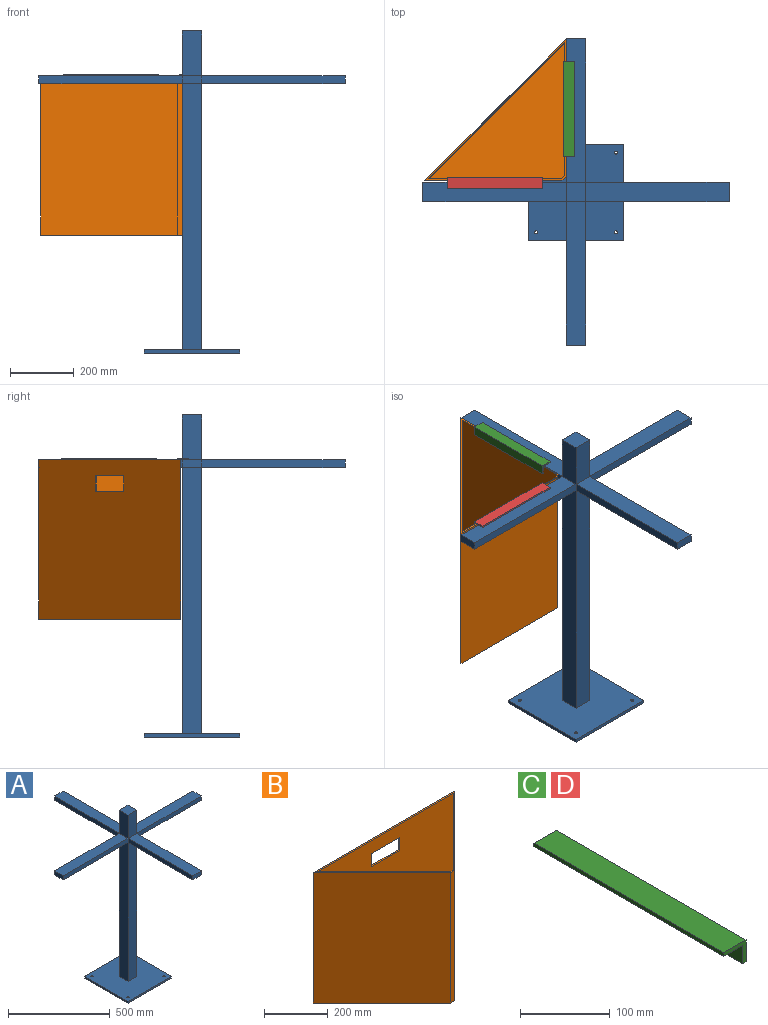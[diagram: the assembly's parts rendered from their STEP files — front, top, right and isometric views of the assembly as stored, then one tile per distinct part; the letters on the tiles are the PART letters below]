
ASSEMBLY  parts=4 mates=3
PART A: 39 faces, bbox 960x960x1010 mm
  f0: plane 835x60mm, normal (0,1,0), area 50100mm2, adj f1,f3,f13,f19
  f1: plane 835x60mm, normal (-1,0,0), area 50100mm2, adj f0,f2,f13,f17
  f2: plane 835x60mm, normal (0,-1,0), area 50100mm2, adj f1,f3,f13,f18
  f3: plane 835x60mm, normal (1,0,0), area 50100mm2, adj f0,f2,f13,f25
  f4: plane 300x10mm, normal (0,1,0), area 3000mm2, adj f5,f11,f12,f13
  f5: plane 300x10mm, normal (-1,0,0), area 3000mm2, adj f4,f6,f12,f13
  f6: plane 300x10mm, normal (0,-1,0), area 3000mm2, adj f5,f11,f12,f13
  f7: cylinder r=5mm len=10mm, axis (0,0,1), area 314.2mm2, adj f12,f13
  f8: cylinder r=5mm len=10mm, axis (0,0,1), area 314.2mm2, adj f12,f13
  f9: cylinder r=5mm len=10mm, axis (0,0,1), area 314.2mm2, adj f12,f13
  f10: cylinder r=5mm len=10mm, axis (0,0,1), area 314.2mm2, adj f12,f13
  f11: plane 300x10mm, normal (1,0,0), area 3000mm2, adj f4,f6,f12,f13
  f12: plane 300x300mm, normal (0,0,-1), area 89685.8mm2, adj f4,f5,f6,f7,f8,f9,f10,f11
  f13: plane 300x300mm, normal (0,0,1), area 86085.8mm2, adj f0,f1,f2,f3,f4,f5,f6,f7
  f14: plane 450x60mm, normal (0,0,1), area 27000mm2, adj f28,f29,f30,f37
  f15: plane 450x60mm, normal (0,0,1), area 27000mm2, adj f20,f21,f26,f36
  f16: plane 450x60mm, normal (0,0,1), area 27000mm2, adj f22,f24,f27,f38
  f17: plane 450x60mm, normal (0,0,-1), area 27000mm2, adj f1,f28,f29,f30
  f18: plane 450x60mm, normal (0,0,-1), area 27000mm2, adj f2,f20,f21,f26
  f19: plane 450x60mm, normal (0,0,-1), area 27000mm2, adj f0,f22,f24,f27
  f20: plane 450x25mm, normal (1,0,0), area 11250mm2, adj f15,f18,f26,f32
  f21: plane 450x25mm, normal (-1,0,0), area 11250mm2, adj f15,f18,f26,f30
  f22: plane 450x25mm, normal (1,0,0), area 11250mm2, adj f16,f19,f27,f31
  f23: plane 450x60mm, normal (0,0,1), area 27000mm2, adj f31,f32,f33,f35
  f24: plane 450x25mm, normal (-1,0,0), area 11250mm2, adj f16,f19,f27,f29
  f25: plane 450x60mm, normal (0,0,-1), area 27000mm2, adj f3,f31,f32,f33
  f26: plane 60x25mm, normal (0,-1,0), area 1500mm2, adj f15,f18,f20,f21
  f27: plane 60x25mm, normal (0,1,0), area 1500mm2, adj f16,f19,f22,f24
  f28: plane 60x25mm, normal (-1,0,0), area 1500mm2, adj f14,f17,f29,f30
  f29: plane 450x25mm, normal (0,1,0), area 11250mm2, adj f14,f17,f24,f28
  f30: plane 450x25mm, normal (0,-1,0), area 11250mm2, adj f14,f17,f21,f28
  f31: plane 450x25mm, normal (0,1,0), area 11250mm2, adj f22,f23,f25,f33
  f32: plane 450x25mm, normal (0,-1,0), area 11250mm2, adj f20,f23,f25,f33
  f33: plane 60x25mm, normal (1,0,0), area 1500mm2, adj f23,f25,f31,f32
  f34: plane 60x60mm, normal (0,0,1), area 3600mm2, adj f35,f36,f37,f38
  f35: plane 140x60mm, normal (1,0,0), area 8400mm2, adj f23,f34,f36,f38
  f36: plane 140x60mm, normal (0,-1,0), area 8400mm2, adj f15,f34,f35,f37
  f37: plane 140x60mm, normal (-1,0,0), area 8400mm2, adj f14,f34,f36,f38
  f38: plane 140x60mm, normal (0,1,0), area 8400mm2, adj f16,f34,f35,f37
PART B: 15 faces, bbox 628.1x304.1x500 mm
  f0: plane 603.97x495mm, normal (0,-1,0), area 292715mm2, adj f3,f7,f8,f10,f11,f12,f13,f14
  f1: plane 628.11x500mm, normal (0,1,0), area 307805.9mm2, adj f4,f6,f8,f9,f10,f11,f12,f13
  f2: plane 495x15.86mm, normal (0,1,0), area 7849.6mm2, adj f3,f7,f8,f14
  f3: plane 495x294.06mm, normal (0.71,0.71,0), area 205849.6mm2, adj f0,f2,f8,f14
  f4: plane 500x304.06mm, normal (-0.71,-0.71,0), area 215000mm2, adj f1,f5,f8,f9
  f5: plane 500x20mm, normal (0,-1,0), area 10000mm2, adj f4,f6,f8,f9
  f6: plane 500x304.06mm, normal (0.71,-0.71,0), area 215000mm2, adj f1,f5,f8,f9
  f7: plane 495x294.06mm, normal (-0.71,0.71,0), area 205849.6mm2, adj f0,f2,f8,f14
  f8: plane 628.11x304.06mm, normal (0,0,1), area 7399.1mm2, adj f0,f1,f2,f3,f4,f5,f6,f7
  f9: plane 628.11x304.06mm, normal (0,0,-1), area 98531.1mm2, adj f1,f4,f5,f6
  f10: plane 125x5mm, normal (0,0,-1), area 625mm2, adj f0,f1,f11,f13
  f11: plane 50x5mm, normal (-1,0,0), area 250mm2, adj f0,f1,f10,f12
  f12: plane 125x5mm, normal (0,0,1), area 625mm2, adj f0,f1,f11,f13
  f13: plane 50x5mm, normal (1,0,0), area 250mm2, adj f0,f1,f10,f12
  f14: plane 603.97x294.06mm, normal (0,0,1), area 91132mm2, adj f0,f2,f3,f7
PART C: 8 faces, bbox 35x300x30 mm
  f0: plane 300x5mm, normal (-1,0,0), area 1500mm2, adj f1,f5,f6,f7
  f1: plane 300x30mm, normal (0,0,-1), area 9000mm2, adj f0,f2,f6,f7
  f2: plane 300x25mm, normal (-1,0,0), area 7500mm2, adj f1,f3,f6,f7
  f3: plane 300x5mm, normal (0,0,-1), area 1500mm2, adj f2,f4,f6,f7
  f4: plane 300x30mm, normal (1,0,0), area 9000mm2, adj f3,f5,f6,f7
  f5: plane 300x35mm, normal (0,0,1), area 10500mm2, adj f0,f4,f6,f7
  f6: plane 35x30mm, normal (0,-1,0), area 300mm2, adj f0,f1,f2,f3,f4,f5
  f7: plane 35x30mm, normal (0,1,0), area 300mm2, adj f0,f1,f2,f3,f4,f5
PART D: same geometry as C
PLACE A t=(139.31,-457.17,-163.31)mm fixed
PLACE B rot(axis=(0,0,1),45deg) t=(-5.26,-306.74,196.69)mm
PLACE C rot(axis=(0,0,1),180deg) t=(116.81,-197.17,686.69)mm
PLACE D rot(axis=(0,0,1),90deg) t=(-114.83,-428.81,686.69)mm
MATE fastened B.f6 <-> A.f24  axis (1,0,0) through (109.31,22.83,696.69)mm
MATE fastened D.f2 <-> B.f3  axis (0,-1,0) through (-114.83,-416.31,696.69)mm
MATE fastened C.f2 <-> B.f7  axis (1,0,0) through (104.31,-197.17,696.69)mm
